# Revit family: Window_Octagon_Vinyl_Harvey
name_source: partatom
category: Windows
units: mm (PartAtom-declared; Revit-internal decimal feet)

## family parameters
Always vertical = Yes
Classification Number = 23.30.20.17.11
Cut with Voids When Loaded = No
Host = Wall
Room Calculation Point = No
Shared = No

## types (1)
- Custom
    AAMA Conformance = As Specified in 08 53 13
    Analytic Construction = <None>
    Assembly Code = B2020100
    CAD Details = https://www.arcat.com
    Define Thermal Properties by = Schematic Type
    Description = Vinyl Window as Specified in 08 53 13
    E283_Air-Infiltration = As Specified in 08 53 13
    E330_Structural-Test-Pressure = As Specified in 08 53 13
    E547_Water-Resistance = As Specified in 08 53 13
    F588_Forced-Entry = As Specified in 08 53 13
    Frame Material = ARCAT - Vinyl - PVC - 0.070" - White
    Glass Thickness = 0' - 0 7/8"
    Glass Type = ARCAT - Glass - Laminated - Clear
    Keynote = 08 53 13
    Manufacturer = Harvey Building Products
    Model = As Specified in 08 53 13
    Operation = As Specified in 08 53 13
    Product Page URL = https://www.arcat.com
    RO Spacing = 0' - 0 5/8"
    Specification = https://www.arcat.com
    URL = https://harveywindows.com
    Wall Closure = By host

## geometry (parser evidence)
native form markers: Sweep x4
no freeform markers — native parametric forms only
